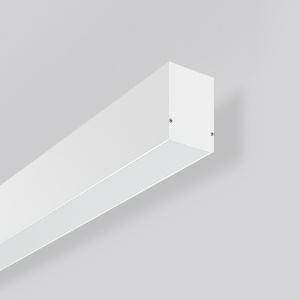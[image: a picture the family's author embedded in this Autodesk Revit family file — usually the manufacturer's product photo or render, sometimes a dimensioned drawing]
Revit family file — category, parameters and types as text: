
# Revit family: less_is_more_50_312610_002_76_d651
name_source: partatom
category: Lighting Fixtures
units: mm (PartAtom-declared; Revit-internal decimal feet)

## family parameters
Cut with Voids When Loaded = No
Host = Face
Light Source = No
Part Type = Normal
Room Calculation Point = No
Round Connector Dimension = Use Diameter
Shared = No

## types (1)
- LESS IS MORE 50 (1 x LED Modul 830, 3250 lm, 3000)
    Apparent Load = 25 VA
    CIE Flux Codes = 48 80 96 50 100
    Color Rendering = 80
    Color Temperature = 3000
    Default Elevation = 1800 mm
    Description = Series: LESS IS MORE 50
Linear wall luminaires. Housing: extruded aluminium profile, powder-coated. End cap aluminium powder-coated. Diffuser made of non-yellowing plastic (PMMA), opal. Direct 50%, indirect 50% light emission. Suitable for Wall (surface). LED unit with integrated converter interchangeable and removable. Suitable for through-wiring. With sensors or as a safety luminaire on request. 
Colour: traffic white, matt (RAL 9016)
Length: 1407 mm
Width: 67 mm
Height: 75 mm
Lamp: LED
Socket: without socket
Colour temperature: 3000K
Colour rendering index (CRI): 80
Light source: LED
Socket lamp2: Without base
Colour temperature: 3000K
Colour rendering index (CRI) 2: 80
System power: 25 W
Rated luminous flux: 3250 lm
Luminous efficiency: 130 lm/W
Control gear: Converter, dimmable, DALI
Control gear: Converter, dimmable, DALI
Protection class: I
Type of protection: IP 20
    Height = 75 mm
    Lamp = 1 x LED Modul 830
    Lamp Light Flux = 3250 lm
    Lamp count = 1
    Length = 1407 mm
    Lifetime = 50000 h
    Luminous efficacy = 130 lm/W
    Manufacturer = RZB
    ModVariant = No
    Model = 312610.002.76
    Mounting Place = Wall
    Mounting Type = Surface mounted
    Number of Poles = 1
    OnlyDefault = Yes
    Power Factor = 1
    Product Name = LESS IS MORE 50
    Product group = Surface mounted LED linear luminaires
    ProductGroupID = 2007
    Protection Class = Protection class I
    Protection Degree = IP 20
    RLX_Detail_Level = 1
    RLX_Emergency_Light_Flux = 0 lm
    RLX_Emergency_Type = 0
    RLX_Emergency_Type_DB = No
    RlxData = <blob elided: 39609 chars, md5=6940532a>
    Socket = socket
    Standby Power = 0 W
    System Light Flux = 3250 lm
    System Power = 25 W
    Type Comments = Product without accessories
    Type Image = 312606.002.jpg
    URL = http://relux.com
    VarID = ---
    Voltage = 0 V
    Weight = 0.00 kg
    Width = 67 mm

## geometry (parser evidence)
native form markers: Blend x4, Sweep x13
no freeform markers — native parametric forms only
